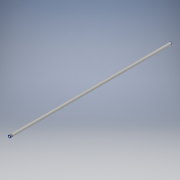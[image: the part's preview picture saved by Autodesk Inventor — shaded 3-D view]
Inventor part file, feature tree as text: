
AUTODESK INVENTOR PART (.ipt)
format: ipt  version: 2019 (Build 230136000, 136)  size: 98,304 bytes
history: native  units: mm
features: extrude x1, other x1, sketch x1
ambient origin geometry x8: Origin, YZ Plane, XZ Plane, XY Plane, X Axis, Y Axis, Z Axis, Center Point
bodies: Solide1 (feature_tree)
feature tree (3):
  extrude  "Extrusion1"  Depth=2.0mm
  other  "Filetage1"
  sketch  "Esquisse1"
